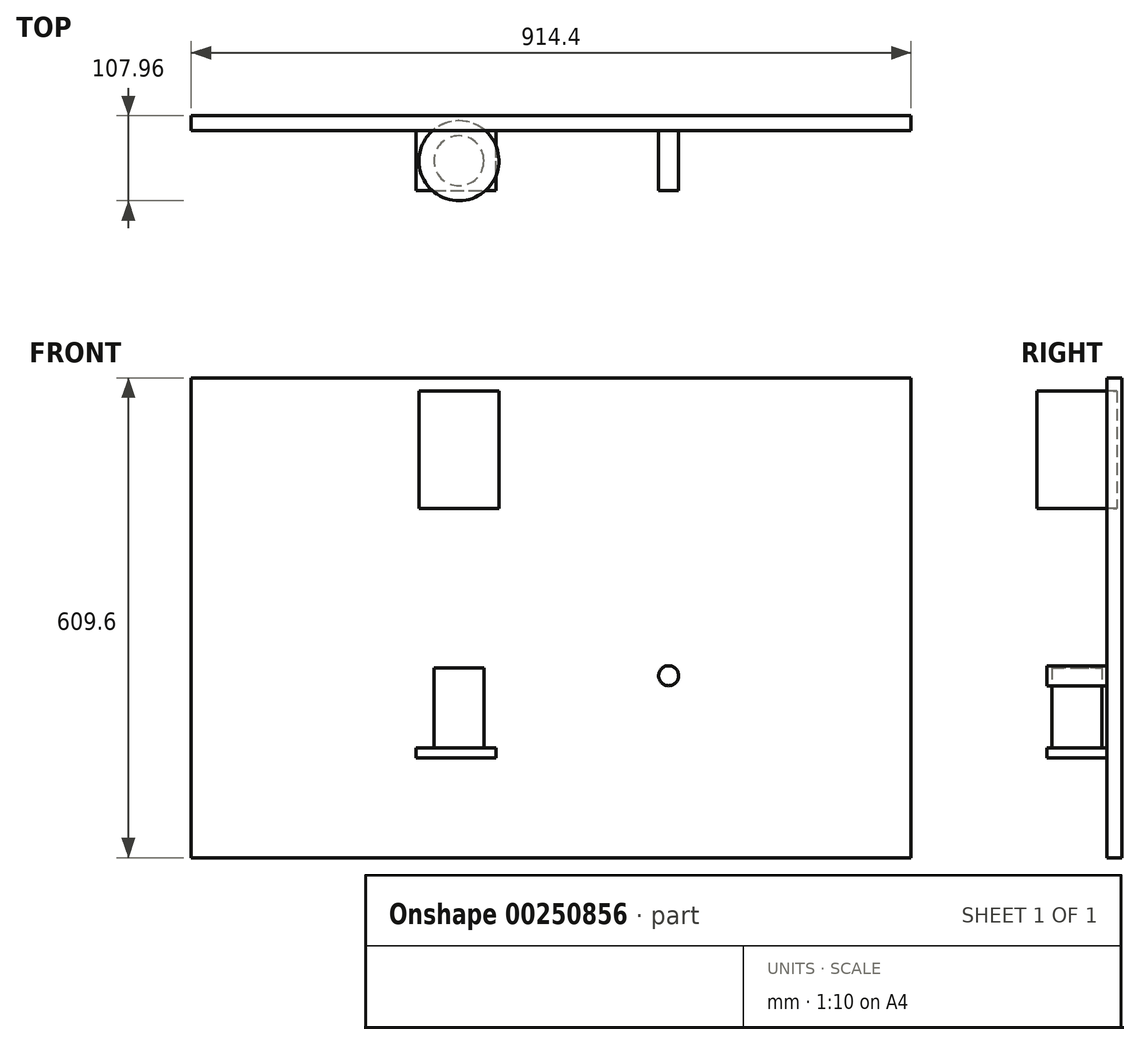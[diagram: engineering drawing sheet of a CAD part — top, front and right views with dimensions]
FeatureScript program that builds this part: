
annotation { "Feature Type Name" : "Feature", "Feature Type Description" : "" }
export const myFeature = defineFeature(function(context is Context, id is Id, definition is map)
    precondition{}
    {
        {
            var Q0;
            Q0=qCreatedBy(makeId("Front.planeOp"),FACE);
            var sketch = newSketch(context, id + "F0", { "sketchPlane" : qUnion([Q0])});
            skLineSegment(sketch, "E0.bottom", {"start": v(457.2, 304.8) * mm, "end": v(-457.2, 304.8) * mm});
            skLineSegment(sketch, "E0.top", {"start": v(457.2, -304.8) * mm, "end": v(-457.2, -304.8) * mm});
            skLineSegment(sketch, "E0.left", {"start": v(457.2, 304.8) * mm, "end": v(457.2, -304.8) * mm});
            skLineSegment(sketch, "E0.right", {"start": v(-457.2, 304.8) * mm, "end": v(-457.2, -304.8) * mm});
            skPoint(sketch, "E0.middle", {"position": v(0, 0) * mm});
            skSolve(sketch);
        }
        {
            var Q0;
            Q0 = qSketchRegion(id + "F0", true);
            extrude(context, id + "F1", {"entities" : qUnion([Q0]), "endBound" : BoundingType.SYMMETRIC, "depth" : 19.05 * mm});
        }
        {
            var Q0;
            Q0=makeQuery(id+"F1.opExtrude","CAP_FACE",FACE,{"disambiguationData":[OSD([sQuery(id+"F0.wireOp",EDGE,"E0.bottom"),sQuery(id+"F0.wireOp",EDGE,"E0.top"),sQuery(id+"F0.wireOp",EDGE,"E0.left"),sQuery(id+"F0.wireOp",EDGE,"E0.right")])],"isStart":false});
            var sketch = newSketch(context, id + "F2", { "sketchPlane" : qUnion([Q0])});
            skLineSegment(sketch, "E1.bottom", {"start": v(-171.75, -165.1) * mm, "end": v(-70.15, -165.1) * mm});
            skLineSegment(sketch, "E1.top", {"start": v(-171.75, -177.8) * mm, "end": v(-70.15, -177.8) * mm});
            skLineSegment(sketch, "E1.left", {"start": v(-171.75, -165.1) * mm, "end": v(-171.75, -177.8) * mm});
            skLineSegment(sketch, "E1.right", {"start": v(-70.15, -165.1) * mm, "end": v(-70.15, -177.8) * mm});
            skSolve(sketch);
        }
        {
            var Q0;
            Q0 = qSketchRegion(id + "F2", true);
            extrude(context, id + "F3", {"entities" : qUnion([Q0]), "depth" : 76.2 * mm});
        }
        {
            var Q0;
            Q0=makeQuery(id+"F3.opExtrude","SWEPT_FACE",FACE,{"disambiguationData":[OSD([sQuery(id+"F2.wireOp",EDGE,"E1.bottom")])]});
            var sketch = newSketch(context, id + "F4", { "sketchPlane" : qUnion([Q0])});
            skCircle(sketch, "E2", {"center": v(-117.3, -47.63) * mm, "radius": 31.75 * mm});
            skPoint(sketch, "E2.centerSnap0", {"position": v(-171.75, -47.63) * mm});
            skLineSegment(sketch, "E3", {"start": v(-117.3, -47.63) * mm, "end": v(-171.75, -47.63) * mm, "construction": true});
            skLineSegment(sketch, "E4", {"start": v(-117.3, -47.63) * mm, "end": v(-117.3, -85.73) * mm, "construction": true});
            skSolve(sketch);
        }
        {
            var Q0;
            Q0=makeQuery(id+"F4.imprint","IMPRINT",FACE,{"disambiguationData":[TD([[makeQuery(id+"F4.imprint","IMPRINT",EDGE,{"derivedFrom":sQuery(id+"F4.wireOp",EDGE,"E2")}),1.0]])]});
            var Q1;
            Q1=sQuery(id+"F4.wireOp",EDGE,"E4");
            var Q2;
            Q2=sQuery(id+"F4.wireOp",EDGE,"E2");
            extrude(context, id + "F5", {"entities" : qUnion([Q0]), "surfaceEntities" : qUnion([Q1, Q2]), "depth" : 101.6 * mm});
        }
        {
            var Q0;
            Q0=makeQuery(id+"F1.opExtrude","CAP_FACE",FACE,{"disambiguationData":[OSD([sQuery(id+"F0.wireOp",EDGE,"E0.bottom"),sQuery(id+"F0.wireOp",EDGE,"E0.top"),sQuery(id+"F0.wireOp",EDGE,"E0.left"),sQuery(id+"F0.wireOp",EDGE,"E0.right")])],"isStart":false});
            var sketch = newSketch(context, id + "F6", { "sketchPlane" : qUnion([Q0])});
            skCircle(sketch, "E5", {"center": v(149.09, -73.57) * mm, "radius": 12.7 * mm});
            skSolve(sketch);
        }
        {
            var Q0;
            Q0 = qSketchRegion(id + "F6", true);
            extrude(context, id + "F7", {"entities" : qUnion([Q0]), "depth" : 76.2 * mm});
        }
        {
            var Q0;
            Q0=makeQuery(id+"F5.opExtrude","CAP_FACE",FACE,{"disambiguationData":[OSD([sQuery(id+"F4.wireOp",EDGE,"E2")])],"isStart":false});
            var sketch = newSketch(context, id + "F8", { "sketchPlane" : qUnion([Q0])});
            skPoint(sketch, "E6", {"position": v(-117.3, -47.63) * mm});
            skSolve(sketch);
        }
        {
            var Q0;
            Q0=qCreatedBy(makeId("Right.planeOp"),FACE);
            var Q1;
            Q1=sQuery(id+"F8.wireOp",VERTEX,"E6");
            cPlane(context, id + "F9", {"entities" : qUnion([Q0, Q1]), "cplaneType" : CPlaneType.PLANE_POINT, "offset" : 25.4 * mm, "width" : 152.4 * mm, "height" : 152.4 * mm});
        }
        {
            var Q0;
            Q0=qCreatedBy(id+"F9.planeOp",FACE);
            var sketch = newSketch(context, id + "F10", { "sketchPlane" : qUnion([Q0])});
            skLineSegment(sketch, "E7", {"start": v(-47.63, -63.5) * mm, "end": v(-47.63, 288.35) * mm, "construction": true});
            skLineSegment(sketch, "E8", {"start": v(-47.63, 288.35) * mm, "end": v(-98.43, 288.35) * mm});
            skLineSegment(sketch, "E9", {"start": v(-98.43, 288.35) * mm, "end": v(-98.43, 139) * mm});
            skLineSegment(sketch, "E10", {"start": v(-98.43, 139) * mm, "end": v(-47.63, 139) * mm});
            skLineSegment(sketch, "E11", {"start": v(-47.63, 288.35) * mm, "end": v(-47.63, 139) * mm});
            skSolve(sketch);
        }
        {
            var Q0;
            Q0 = qSketchRegion(id + "F10", true);
            var Q1;
            Q1=sQuery(id+"F10.wireOp",EDGE,"E7");
            revolve(context, id + "F11", {"entities" : qUnion([Q0]), "axis" : qUnion([Q1]), "revolveType" : RevolveType.FULL});
        }
    });
